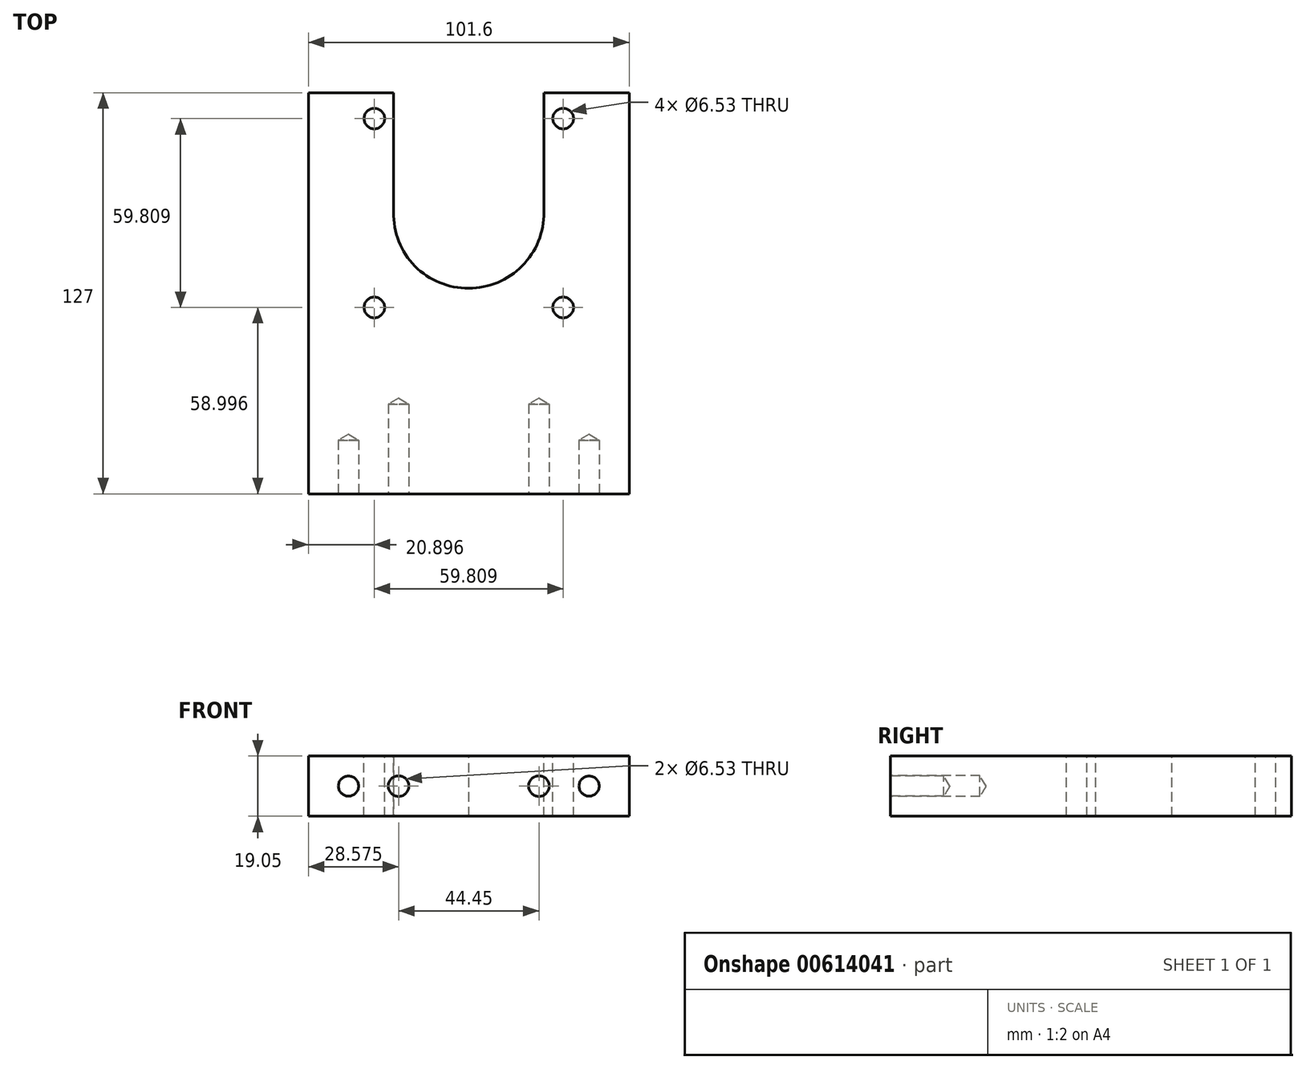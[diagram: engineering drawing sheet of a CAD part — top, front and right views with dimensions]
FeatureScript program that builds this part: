
annotation { "Feature Type Name" : "Feature", "Feature Type Description" : "" }
export const myFeature = defineFeature(function(context is Context, id is Id, definition is map)
    precondition{}
    {
        {
            var Q0;
            Q0=qCreatedBy(makeId("Top.planeOp"),FACE);
            var sketch = newSketch(context, id + "F0", { "sketchPlane" : qUnion([Q0])});
            skLineSegment(sketch, "E0.bottom", {"start": v(-50.8, 88.9) * mm, "end": v(50.8, 88.9) * mm});
            skLineSegment(sketch, "E0.top", {"start": v(-50.8, -63.5) * mm, "end": v(50.8, -63.5) * mm});
            skLineSegment(sketch, "E0.left", {"start": v(-50.8, 88.9) * mm, "end": v(-50.8, -63.5) * mm});
            skLineSegment(sketch, "E0.right", {"start": v(50.8, 88.9) * mm, "end": v(50.8, -63.5) * mm});
            skSolve(sketch);
        }
        {
            var Q0;
            Q0 = qSketchRegion(id + "F0", true);
            extrude(context, id + "F1", {"entities" : qUnion([Q0]), "depth" : 19.05 * mm, "offsetDistance" : 25.4 * mm});
        }
        {
            var Q0;
            Q0=makeQuery(id+"F1.opExtrude","CAP_FACE",FACE,{"disambiguationData":[OSD([sQuery(id+"F0.wireOp",EDGE,"E0.bottom"),sQuery(id+"F0.wireOp",EDGE,"E0.top"),sQuery(id+"F0.wireOp",EDGE,"E0.left"),sQuery(id+"F0.wireOp",EDGE,"E0.right")])],"isStart":false});
            var sketch = newSketch(context, id + "F2", { "sketchPlane" : qUnion([Q0])});
            skPoint(sketch, "E1", {"position": v(0, 25.4) * mm});
            skCircle(sketch, "E2", {"center": v(0, 25.4) * mm, "radius": 42.3 * mm, "construction": true});
            skPoint(sketch, "E3", {"position": v(-29.9, 55.3) * mm});
            skPoint(sketch, "E4", {"position": v(29.9, 55.3) * mm});
            skPoint(sketch, "E5", {"position": v(29.9, -4.5) * mm});
            skPoint(sketch, "E6", {"position": v(-29.9, -4.5) * mm});
            skLineSegment(sketch, "E7", {"start": v(0, 25.4) * mm, "end": v(-29.9, 55.3) * mm, "construction": true});
            skLineSegment(sketch, "E8", {"start": v(0, 25.4) * mm, "end": v(29.9, 55.3) * mm, "construction": true});
            skLineSegment(sketch, "E9", {"start": v(0, 25.4) * mm, "end": v(29.9, -4.5) * mm, "construction": true});
            skLineSegment(sketch, "E10", {"start": v(0, 25.4) * mm, "end": v(-29.9, -4.5) * mm, "construction": true});
            skCircle(sketch, "E11", {"center": v(0, 25.4) * mm, "radius": 23.81 * mm});
            skSolve(sketch);
        }
        {
            var Q0;
            Q0=sQuery(id+"F2.wireOp",VERTEX,"E3");
            var Q1;
            Q1=sQuery(id+"F2.wireOp",VERTEX,"E4");
            var Q2;
            Q2=sQuery(id+"F2.wireOp",VERTEX,"E5");
            var Q3;
            Q3=sQuery(id+"F2.wireOp",VERTEX,"E6");
            var Q4;
            Q4=makeQuery(id+"F1.opExtrude","SWEPT_BODY",BODY,{"disambiguationData":[OSD([sQuery(id+"F0.wireOp",EDGE,"E0.bottom"),sQuery(id+"F0.wireOp",EDGE,"E0.top"),sQuery(id+"F0.wireOp",EDGE,"E0.left"),sQuery(id+"F0.wireOp",EDGE,"E0.right")])]});
            hole(context, id + "F3", {"style" : HoleStyle.SIMPLE, "endStyle" : HoleEndStyle.THROUGH, "standardTappedOrClearance" : lookupTablePath({ "standard" : "ANSI", "fit" : "Close", "size" : "1/4", "type" : "Clearance" }), "standardBlindInLast" : lookupTablePath({ "fit" : "Close", "standard" : "ANSI", "size" : "1/4", "type" : "Clearance" }), "holeDiameter" : 6.53 * mm, "majorDiameter" : 6.35 * mm, "tappedDepth" : 19.05 * mm, "tapClearance" : 3, "startFromSketch" : true, "locations" : qUnion([Q0, Q1, Q2, Q3]), "scope" : qUnion([Q4])});
        }
        {
            var Q0;
            Q0 = qSketchRegion(id + "F2", true);
            extrude(context, id + "F4", {"entities" : qUnion([Q0]), "operationType" : NewBodyOperationType.REMOVE, "endBound" : BoundingType.THROUGH_ALL, "oppositeDirection" : true, "depth" : 25.4 * mm, "offsetDistance" : 25.4 * mm});
        }
        {
            var Q0;
            Q0=makeQuery(id+"F1.opExtrude","CAP_FACE",FACE,{"disambiguationData":[OSD([sQuery(id+"F0.wireOp",EDGE,"E0.bottom"),sQuery(id+"F0.wireOp",EDGE,"E0.top"),sQuery(id+"F0.wireOp",EDGE,"E0.left"),sQuery(id+"F0.wireOp",EDGE,"E0.right")])],"isStart":false});
            var sketch = newSketch(context, id + "F5", { "sketchPlane" : qUnion([Q0])});
            skLineSegment(sketch, "E12", {"start": v(-23.81, 25.7) * mm, "end": v(-23.81, 88.9) * mm});
            skLineSegment(sketch, "E13", {"start": v(23.81, 25.68) * mm, "end": v(23.81, 88.9) * mm});
            skLineSegment(sketch, "E14", {"start": v(23.81, 88.9) * mm, "end": v(-23.81, 88.9) * mm});
            skArc(sketch, "E15", {"start": v(23.81, 25.68) * mm, "mid": v(16.85, 8.74) * mm, "end": v(0, 1.59) * mm});
            skArc(sketch, "E16", {"start": v(0, 1.59) * mm, "mid": v(-17.02, 8.58) * mm, "end": v(-23.81, 25.7) * mm});
            skSolve(sketch);
        }
        {
            var Q0;
            Q0 = qSketchRegion(id + "F5", true);
            extrude(context, id + "F6", {"entities" : qUnion([Q0]), "operationType" : NewBodyOperationType.REMOVE, "endBound" : BoundingType.THROUGH_ALL, "oppositeDirection" : true, "depth" : 25.4 * mm, "offsetDistance" : 25.4 * mm});
        }
        {
            var Q0;
            Q0=makeQuery(id+"F1.opExtrude","CAP_FACE",FACE,{"disambiguationData":[OSD([sQuery(id+"F0.wireOp",EDGE,"E0.bottom"),sQuery(id+"F0.wireOp",EDGE,"E0.top"),sQuery(id+"F0.wireOp",EDGE,"E0.left"),sQuery(id+"F0.wireOp",EDGE,"E0.right")])],"isStart":false});
            var sketch = newSketch(context, id + "F7", { "sketchPlane" : qUnion([Q0])});
            skLineSegment(sketch, "E17", {"start": v(-50.8, 63.5) * mm, "end": v(50.8, 63.5) * mm});
            skLineSegment(sketch, "E18", {"start": v(-50.8, 88.9) * mm, "end": v(50.8, 88.9) * mm});
            skLineSegment(sketch, "E19", {"start": v(50.8, 88.9) * mm, "end": v(50.8, 63.5) * mm});
            skLineSegment(sketch, "E20", {"start": v(-50.8, 63.5) * mm, "end": v(-50.8, 88.9) * mm});
            skSolve(sketch);
        }
        {
            var Q0;
            Q0 = qSketchRegion(id + "F7", true);
            extrude(context, id + "F8", {"entities" : qUnion([Q0]), "operationType" : NewBodyOperationType.REMOVE, "endBound" : BoundingType.THROUGH_ALL, "oppositeDirection" : true, "depth" : 25.4 * mm, "offsetDistance" : 25.4 * mm});
        }
        {
            var Q0;
            Q0=makeQuery(id+"F1.opExtrude","SWEPT_FACE",FACE,{"disambiguationData":[OSD([sQuery(id+"F0.wireOp",EDGE,"E0.top")])]});
            var sketch = newSketch(context, id + "F9", { "sketchPlane" : qUnion([Q0])});
            skLineSegment(sketch, "E21", {"start": v(-50.8, 9.53) * mm, "end": v(50.8, 9.53) * mm, "construction": true});
            skPoint(sketch, "E22", {"position": v(-38.1, 9.53) * mm});
            skPoint(sketch, "E23", {"position": v(-22.23, 9.53) * mm});
            skPoint(sketch, "E24", {"position": v(22.23, 9.53) * mm});
            skPoint(sketch, "E25", {"position": v(38.1, 9.53) * mm});
            skSolve(sketch);
        }
        {
            var Q0;
            Q0=sQuery(id+"F9.wireOp",VERTEX,"E22");
            var Q1;
            Q1=sQuery(id+"F9.wireOp",VERTEX,"E25");
            var Q2;
            Q2=makeQuery(id+"F1.opExtrude","SWEPT_BODY",BODY,{"disambiguationData":[OSD([sQuery(id+"F0.wireOp",EDGE,"E0.bottom"),sQuery(id+"F0.wireOp",EDGE,"E0.top"),sQuery(id+"F0.wireOp",EDGE,"E0.left"),sQuery(id+"F0.wireOp",EDGE,"E0.right")])]});
            hole(context, id + "F10", {"style" : HoleStyle.SIMPLE, "endStyle" : HoleEndStyle.BLIND, "holeDiameter" : 6.38 * mm, "majorDiameter" : 6.35 * mm, "holeDepth" : 16.94 * mm, "tappedDepth" : 19.05 * mm, "tapClearance" : 3, "startFromSketch" : true, "locations" : qUnion([Q0, Q1]), "scope" : qUnion([Q2])});
        }
        {
            var Q0;
            Q0=sQuery(id+"F9.wireOp",VERTEX,"E23");
            var Q1;
            Q1=sQuery(id+"F9.wireOp",VERTEX,"E24");
            var Q2;
            Q2=makeQuery(id+"F1.opExtrude","SWEPT_BODY",BODY,{"disambiguationData":[OSD([sQuery(id+"F0.wireOp",EDGE,"E0.bottom"),sQuery(id+"F0.wireOp",EDGE,"E0.top"),sQuery(id+"F0.wireOp",EDGE,"E0.left"),sQuery(id+"F0.wireOp",EDGE,"E0.right")])]});
            hole(context, id + "F11", {"style" : HoleStyle.SIMPLE, "endStyle" : HoleEndStyle.BLIND, "standardTappedOrClearance" : lookupTablePath({ "standard" : "ANSI", "engagement" : "75%", "pitch" : "18 tpi", "size" : "5/16", "type" : "Tapped" }), "standardBlindInLast" : lookupTablePath({ "standard" : "ANSI", "engagement" : "75%", "pitch" : "18 tpi", "size" : "5/16", "type" : "Tapped" }), "holeDiameter" : 6.53 * mm, "majorDiameter" : 7.94 * mm, "showTappedDepth" : true, "holeDepth" : 28.36 * mm, "tappedDepth" : 24.13 * mm, "tapClearance" : 3, "startFromSketch" : true, "locations" : qUnion([Q0, Q1]), "scope" : qUnion([Q2])});
        }
    });
